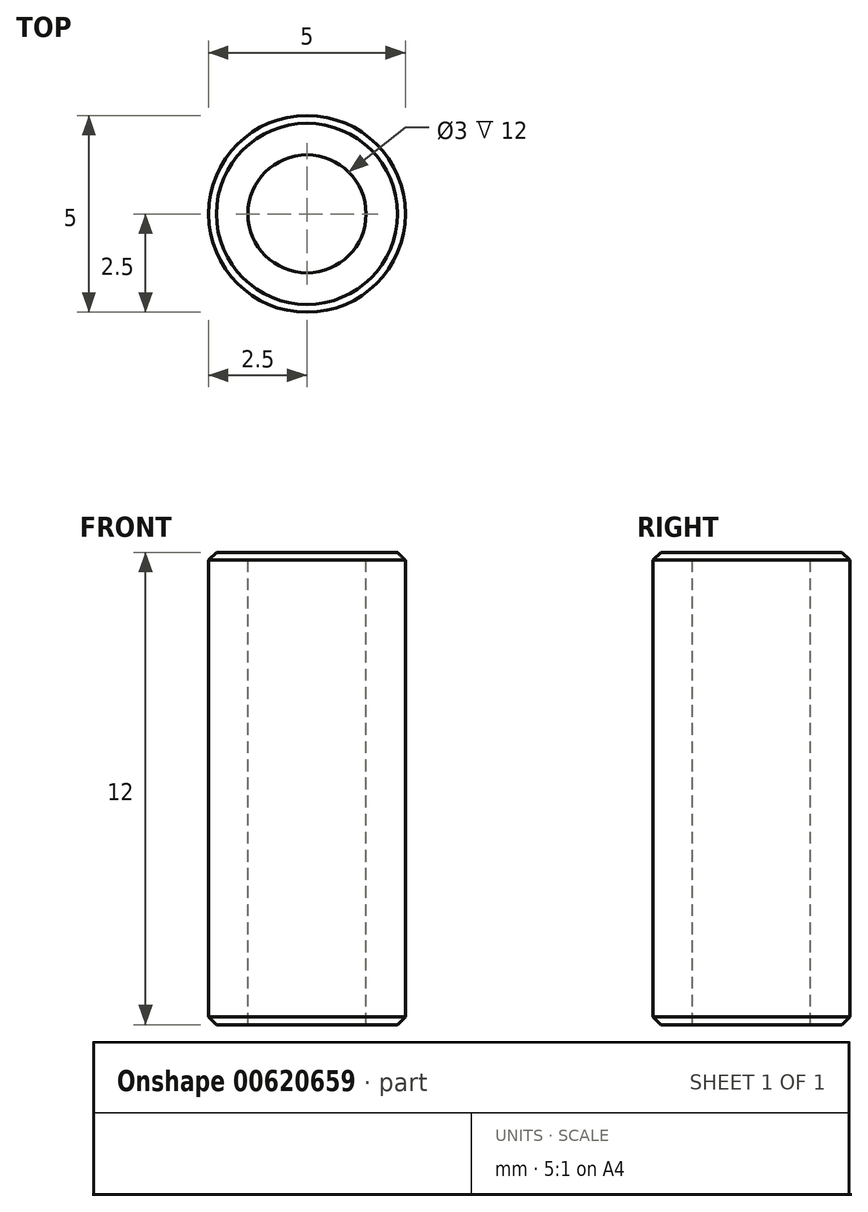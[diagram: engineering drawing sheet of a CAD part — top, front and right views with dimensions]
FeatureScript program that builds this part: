
annotation { "Feature Type Name" : "Feature", "Feature Type Description" : "" }
export const myFeature = defineFeature(function(context is Context, id is Id, definition is map)
    precondition{}
    {
        {
            var Q0;
            Q0=qCreatedBy(makeId("Top.planeOp"),FACE);
            var sketch = newSketch(context, id + "F0", { "sketchPlane" : qUnion([Q0])});
            skCircle(sketch, "E0", {"center": v(0, 0) * mm, "radius": 2.5 * mm});
            skSolve(sketch);
        }
        {
            var Q0;
            Q0=qSketchRegion(id+"F0",true);
            extrude(context, id + "F1", {"entities" : qUnion([Q0]), "depth" : 12 * mm});
        }
        {
            var Q0;
            Q0=makeQuery(id+"F1.opExtrude","CAP_FACE",FACE,{"disambiguationData":[OSD([sQuery(id+"F0.wireOp",EDGE,"E0")])],"isStart":false});
            var Q1;
            Q1=makeQuery(id+"F1.opExtrude","CAP_FACE",FACE,{"disambiguationData":[OSD([sQuery(id+"F0.wireOp",EDGE,"E0")])],"isStart":true});
            chamfer(context, id + "F2", {"entities" : qUnion([Q0, Q1]), "width" : 0.2 * mm, "tangentPropagation" : true});
        }
        {
            var Q0;
            Q0=sQuery(id+"F0.wireOp",VERTEX,"E0.center");
            var Q1;
            Q1=makeQuery(id+"F1.opExtrude","SWEPT_BODY",BODY,{"disambiguationData":[OSD([sQuery(id+"F0.wireOp",EDGE,"E0")])]});
            hole(context, id + "F3", {"style" : HoleStyle.SIMPLE, "endStyle" : HoleEndStyle.THROUGH, "oppositeDirection" : true, "holeDiameter" : 3 * mm, "isTappedThrough" : true, "tappedDepth" : 12 * mm, "tapClearance" : 3, "locations" : qUnion([Q0]), "scope" : qUnion([Q1]), "startStyle" : HoleStartStyle.SKETCH});
        }
    });
